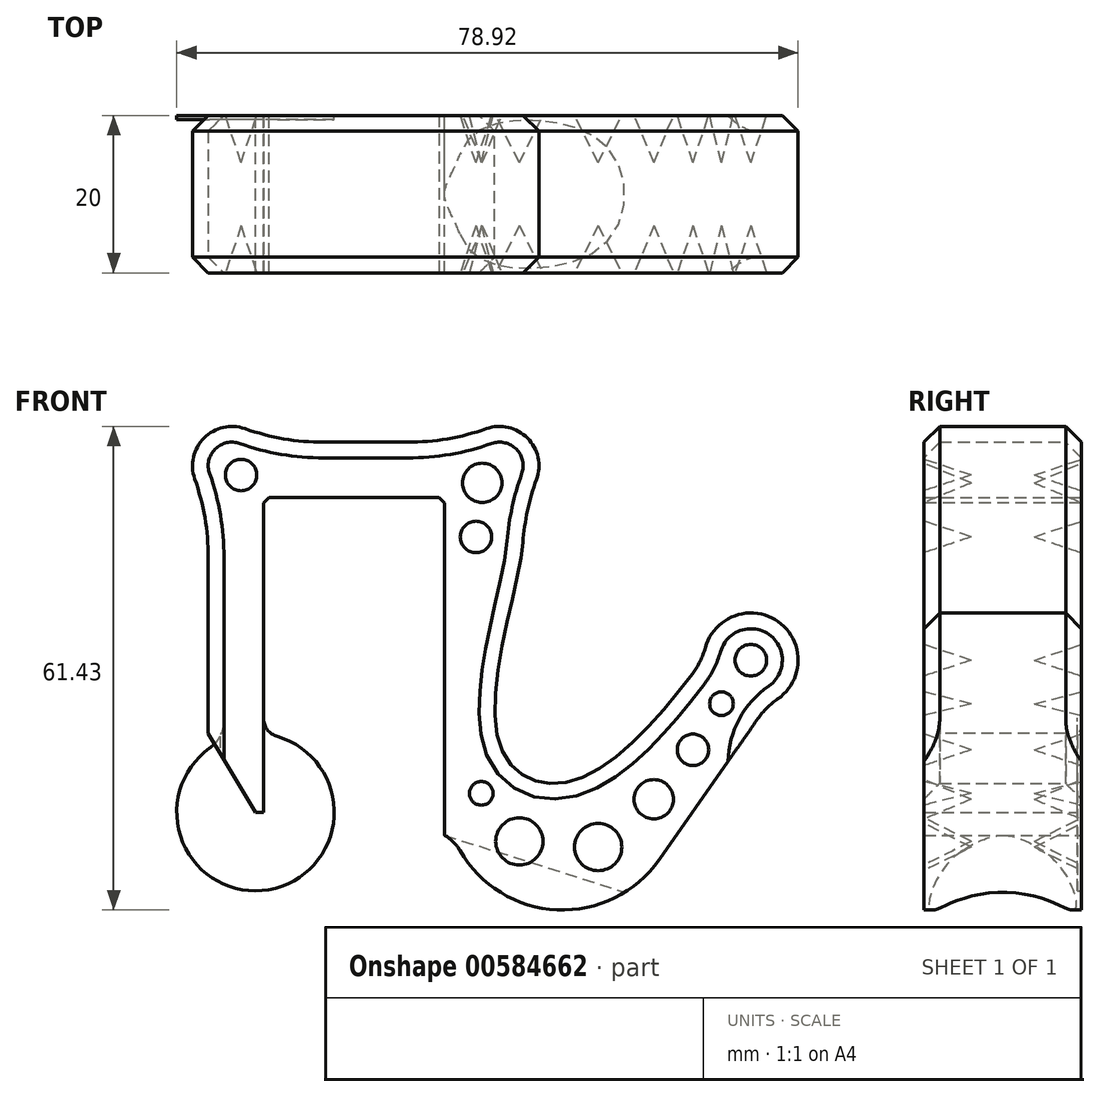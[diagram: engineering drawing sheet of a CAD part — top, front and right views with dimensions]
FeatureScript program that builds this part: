
annotation { "Feature Type Name" : "Feature", "Feature Type Description" : "" }
export const myFeature = defineFeature(function(context is Context, id is Id, definition is map)
    precondition{}
    {
        {
            var Q0;
            Q0=qCreatedBy(makeId("Front.planeOp"),FACE);
            var sketch = newSketch(context, id + "F0", { "sketchPlane" : qUnion([Q0])});
            skLineSegment(sketch, "E0", {"start": v(0, 0) * mm, "end": v(0, 40) * mm});
            skLineSegment(sketch, "E1", {"start": v(0, 40) * mm, "end": v(23, 40) * mm});
            skLineSegment(sketch, "E2", {"start": v(23, 40) * mm, "end": v(23, 2.57) * mm});
            skLineSegment(sketch, "E3", {"start": v(0, 0) * mm, "end": v(-7, 0) * mm});
            skLineSegment(sketch, "E4", {"start": v(-7, 0) * mm, "end": v(-7, 47) * mm});
            skLineSegment(sketch, "E5", {"start": v(-7, 47) * mm, "end": v(33, 47) * mm});
            skLineSegment(sketch, "E6", {"start": v(33, 47) * mm, "end": v(33, 35) * mm});
            skCircle(sketch, "E7", {"center": v(-4, 44) * mm, "radius": 5 * mm});
            skCircle(sketch, "E8", {"center": v(30, 44) * mm, "radius": 5 * mm});
            skLineSegment(sketch, "E9", {"start": v(66.02, 16.44) * mm, "end": v(50.29, -6.03) * mm});
            skCircle(sketch, "E10", {"center": v(61.92, 19.3) * mm, "radius": 6 * mm});
            skPoint(sketch, "E10.second.point", {"position": v(57, 22.75) * mm});
            skPoint(sketch, "E10.third.point", {"position": v(65.36, 24.22) * mm});
            skLineSegment(sketch, "E11", {"start": v(61.92, 19.3) * mm, "end": v(66.02, 16.44) * mm, "construction": true});
            skLineSegment(sketch, "E12", {"start": v(57, 22.75) * mm, "end": v(61.92, 19.3) * mm, "construction": true});
            skLineSegment(sketch, "E13", {"start": v(65.36, 24.22) * mm, "end": v(61.92, 19.3) * mm, "construction": true});
            skFitSpline(sketch, "E14", {"points": [v(33, 35) * mm, v(29.83, 9.17) * mm, v(39.83, 4.17) * mm, v(57.83, 22.17) * mm], "startDerivative": vector(0, -39.67) * mm, "endDerivative": vector(32.2, 46) * mm});
            skPoint(sketch, "E15.visualSharp", {"position": v(23, -45) * mm});
            skArc(sketch, "E15.filletArc", {"start": v(23, 2.57) * mm, "mid": v(33.49, -11.73) * mm, "end": v(50.29, -6.03) * mm});
            skPoint(sketch, "E16", {"position": v(0, 47) * mm});
            skLineSegment(sketch, "E17", {"start": v(53.81, 16.44) * mm, "end": v(57.83, 22.17) * mm, "construction": true});
            skLineSegment(sketch, "E18", {"start": v(33, 30) * mm, "end": v(33, 35) * mm, "construction": true});
            skLineSegment(sketch, "E19", {"start": v(12, -11) * mm, "end": v(50.15, -23.03) * mm});
            skLineSegment(sketch, "E20", {"start": v(50.15, -23.03) * mm, "end": v(53.46, -12.54) * mm});
            skLineSegment(sketch, "E21", {"start": v(53.46, -12.54) * mm, "end": v(15.3, -0.5) * mm});
            skLineSegment(sketch, "E22", {"start": v(15.3, -0.5) * mm, "end": v(12, -11) * mm});
            skLineSegment(sketch, "E23", {"start": v(12, -11) * mm, "end": v(12, 0) * mm, "construction": true});
            skLineSegment(sketch, "E24", {"start": v(23, 2.57) * mm, "end": v(23, -12.43) * mm});
            skLineSegment(sketch, "E25", {"start": v(23, -12.43) * mm, "end": v(25, -12.43) * mm});
            skArc(sketch, "E26", {"start": v(30.06, -10.15) * mm, "mid": v(27.19, -10.52) * mm, "end": v(25, -12.43) * mm});
            skSolve(sketch);
        }
        {
            var Q0;
            {var subQ0=sQuery(id+"F0.wireOp",EDGE,"E5");var subQ1=sQuery(id+"F0.wireOp",EDGE,"E4");var subQ2=makeQuery(id+"F0.imprint","INTERSECT",VERTEX,{"derivedFrom":[subQ1,subQ0]});Q0=makeQuery(id+"F0.imprint","IMPRINT",FACE,{"disambiguationData":[TD([[makeQuery(id+"F0.imprint","IMPRINT",EDGE,{"disambiguationData":[TD([[subQ2,1.0]])],"derivedFrom":subQ1}),1.0]])]});}
            var Q1;
            {var subQ0=sQuery(id+"F0.wireOp",EDGE,"E6");var subQ1=sQuery(id+"F0.wireOp",EDGE,"E5");var subQ2=makeQuery(id+"F0.imprint","INTERSECT",VERTEX,{"derivedFrom":[subQ1,subQ0]});Q1=makeQuery(id+"F0.imprint","IMPRINT",FACE,{"disambiguationData":[TD([[makeQuery(id+"F0.imprint","IMPRINT",EDGE,{"disambiguationData":[TD([[subQ2,1.0]])],"derivedFrom":subQ1}),1.0]])]});}
            var Q2;
            {var subQ0=sQuery(id+"F0.wireOp",EDGE,"E10");var subQ1=makeQuery(id+"F0.imprint","INTERSECT",VERTEX,{"derivedFrom":[sQuery(id+"F0.wireOp",EDGE,"E9"),subQ0]});Q2=makeQuery(id+"F0.imprint","IMPRINT",FACE,{"disambiguationData":[TD([[makeQuery(id+"F0.imprint","IMPRINT",EDGE,{"disambiguationData":[TD([[subQ1,1.0]])],"derivedFrom":subQ0}),1.0]])]});}
            var Q3;
            {var subQ0=sQuery(id+"F0.wireOp",EDGE,"E15.filletArc");Q3=makeQuery(id+"F0.imprint","IMPRINT",FACE,{"disambiguationData":[TD([[makeQuery(id+"F0.imprint","IMPRINT",EDGE,{"derivedFrom":subQ0}),1.0]])]});}
            var Q4;
            {var subQ0=sQuery(id+"F0.wireOp",EDGE,"E5");var subQ1=sQuery(id+"F0.wireOp",EDGE,"E4");var subQ2=makeQuery(id+"F0.imprint","INTERSECT",VERTEX,{"derivedFrom":[subQ1,subQ0]});Q4=makeQuery(id+"F0.imprint","IMPRINT",FACE,{"disambiguationData":[TD([[makeQuery(id+"F0.imprint","IMPRINT",EDGE,{"disambiguationData":[TD([[subQ2,1.0]])],"derivedFrom":subQ1}),-1.0]])]});}
            var Q5;
            {var subQ0=sQuery(id+"F0.wireOp",EDGE,"E6");var subQ1=sQuery(id+"F0.wireOp",EDGE,"E5");var subQ2=makeQuery(id+"F0.imprint","INTERSECT",VERTEX,{"derivedFrom":[subQ1,subQ0]});Q5=makeQuery(id+"F0.imprint","IMPRINT",FACE,{"disambiguationData":[TD([[makeQuery(id+"F0.imprint","IMPRINT",EDGE,{"disambiguationData":[TD([[subQ2,1.0]])],"derivedFrom":subQ1}),-1.0]])]});}
            var Q6;
            Q6=makeQuery(id+"F0.imprint","IMPRINT",FACE,{"disambiguationData":[TD([[makeQuery(id+"F0.imprint","IMPRINT",EDGE,{"derivedFrom":sQuery(id+"F0.wireOp",EDGE,"E0")}),1.0]])]});
            var Q7;
            {var subQ0=sQuery(id+"F0.wireOp",EDGE,"E24");var subQ3=sQuery(id+"F0.wireOp",EDGE,"E21");var subQ5=makeQuery(id+"F0.imprint","INTERSECT",VERTEX,{"derivedFrom":[subQ3,subQ0]});Q7=makeQuery(id+"F0.imprint","IMPRINT",FACE,{"disambiguationData":[TD([[makeQuery(id+"F0.imprint","IMPRINT",EDGE,{"disambiguationData":[TD([[subQ5,1.0]])],"derivedFrom":subQ3}),-1.0]])]});}
            extrude(context, id + "F1", {"entities" : qUnion([Q0, Q1, Q2, Q3, Q4, Q5, Q6, Q7]), "endBound" : BoundingType.SYMMETRIC, "depth" : 20 * mm, "offsetDistance" : 25 * mm});
        }
        {
            var Q0;
            Q0=makeQuery(id+"F1.opExtrude","SWEPT_EDGE",EDGE,{"disambiguationData":[OSD([sQuery(id+"F0.wireOp",EDGE,"E4"),sQuery(id+"F0.wireOp",EDGE,"E7")])]});
            var Q1;
            Q1=makeQuery(id+"F1.opExtrude","SWEPT_EDGE",EDGE,{"disambiguationData":[OSD([sQuery(id+"F0.wireOp",EDGE,"E5"),sQuery(id+"F0.wireOp",EDGE,"E7")])]});
            var Q2;
            Q2=makeQuery(id+"F1.opExtrude","SWEPT_EDGE",EDGE,{"disambiguationData":[OSD([sQuery(id+"F0.wireOp",EDGE,"E5"),sQuery(id+"F0.wireOp",EDGE,"E8")])]});
            var Q3;
            Q3=makeQuery(id+"F1.opExtrude","SWEPT_EDGE",EDGE,{"disambiguationData":[OSD([sQuery(id+"F0.wireOp",EDGE,"E6"),sQuery(id+"F0.wireOp",EDGE,"E8")])]});
            fillet(context, id + "F2", {"entities" : qUnion([Q0, Q1, Q2, Q3]), "radius" : 30 * mm, "tangentPropagation" : true, "allowEdgeOverflow" : false});
        }
        {
            var Q0;
            Q0=makeQuery(id+"F1.opExtrude","SWEPT_EDGE",EDGE,{"disambiguationData":[OSD([sQuery(id+"F0.wireOp",EDGE,"E10"),sQuery(id+"F0.wireOp",EDGE,"E14")])]});
            var Q1;
            Q1=makeQuery(id+"F1.opExtrude","SWEPT_EDGE",EDGE,{"disambiguationData":[OSD([sQuery(id+"F0.wireOp",EDGE,"E9"),sQuery(id+"F0.wireOp",EDGE,"E10")])]});
            fillet(context, id + "F3", {"entities" : qUnion([Q0, Q1]), "radius" : 10 * mm, "tangentPropagation" : true, "allowEdgeOverflow" : false});
        }
        {
            var Q0;
            {var subQ0=sQuery(id+"F0.wireOp",EDGE,"E7");var subQ1=sQuery(id+"F0.wireOp",EDGE,"E4");Q0=makeQuery(id+"F2.opFillet","BLEND_EDGE",EDGE,{"blendedFrom":[makeQuery(id+"F1.opExtrude","SWEPT_EDGE",EDGE,{"disambiguationData":[OSD([subQ1,subQ0])]}),makeQuery(id+"F1.opExtrude","CAP_FACE",FACE,{"disambiguationData":[OSD([sQuery(id+"F0.wireOp",EDGE,"E0"),sQuery(id+"F0.wireOp",EDGE,"E1"),sQuery(id+"F0.wireOp",EDGE,"E2"),sQuery(id+"F0.wireOp",EDGE,"E3"),subQ1,sQuery(id+"F0.wireOp",EDGE,"E5"),sQuery(id+"F0.wireOp",EDGE,"E6"),subQ0,sQuery(id+"F0.wireOp",EDGE,"E8"),sQuery(id+"F0.wireOp",EDGE,"E9"),sQuery(id+"F0.wireOp",EDGE,"E10"),sQuery(id+"F0.wireOp",EDGE,"E14"),sQuery(id+"F0.wireOp",EDGE,"E15.filletArc")])],"isStart":false})],"blendedInto":[makeQuery(id+"F1.opExtrude","CAP_FACE",FACE,{"disambiguationData":[OSD([sQuery(id+"F0.wireOp",EDGE,"E0"),sQuery(id+"F0.wireOp",EDGE,"E1"),sQuery(id+"F0.wireOp",EDGE,"E2"),sQuery(id+"F0.wireOp",EDGE,"E3"),subQ1,sQuery(id+"F0.wireOp",EDGE,"E5"),sQuery(id+"F0.wireOp",EDGE,"E6"),subQ0,sQuery(id+"F0.wireOp",EDGE,"E8"),sQuery(id+"F0.wireOp",EDGE,"E9"),sQuery(id+"F0.wireOp",EDGE,"E10"),sQuery(id+"F0.wireOp",EDGE,"E14"),sQuery(id+"F0.wireOp",EDGE,"E15.filletArc")])],"isStart":false})]});}
            var Q1;
            {var subQ0=sQuery(id+"F0.wireOp",EDGE,"E7");var subQ1=sQuery(id+"F0.wireOp",EDGE,"E4");Q1=makeQuery(id+"F2.opFillet","BLEND_EDGE",EDGE,{"blendedFrom":[makeQuery(id+"F1.opExtrude","SWEPT_EDGE",EDGE,{"disambiguationData":[OSD([subQ1,subQ0])]}),makeQuery(id+"F1.opExtrude","CAP_FACE",FACE,{"disambiguationData":[OSD([sQuery(id+"F0.wireOp",EDGE,"E0"),sQuery(id+"F0.wireOp",EDGE,"E1"),sQuery(id+"F0.wireOp",EDGE,"E2"),sQuery(id+"F0.wireOp",EDGE,"E3"),subQ1,sQuery(id+"F0.wireOp",EDGE,"E5"),sQuery(id+"F0.wireOp",EDGE,"E6"),subQ0,sQuery(id+"F0.wireOp",EDGE,"E8"),sQuery(id+"F0.wireOp",EDGE,"E9"),sQuery(id+"F0.wireOp",EDGE,"E10"),sQuery(id+"F0.wireOp",EDGE,"E14"),sQuery(id+"F0.wireOp",EDGE,"E15.filletArc")])],"isStart":true})],"blendedInto":[makeQuery(id+"F1.opExtrude","CAP_FACE",FACE,{"disambiguationData":[OSD([sQuery(id+"F0.wireOp",EDGE,"E0"),sQuery(id+"F0.wireOp",EDGE,"E1"),sQuery(id+"F0.wireOp",EDGE,"E2"),sQuery(id+"F0.wireOp",EDGE,"E3"),subQ1,sQuery(id+"F0.wireOp",EDGE,"E5"),sQuery(id+"F0.wireOp",EDGE,"E6"),subQ0,sQuery(id+"F0.wireOp",EDGE,"E8"),sQuery(id+"F0.wireOp",EDGE,"E9"),sQuery(id+"F0.wireOp",EDGE,"E10"),sQuery(id+"F0.wireOp",EDGE,"E14"),sQuery(id+"F0.wireOp",EDGE,"E15.filletArc")])],"isStart":true})]});}
            var Q2;
            Q2=makeQuery(id+"F1.opExtrude","CAP_EDGE",EDGE,{"disambiguationData":[OSD([sQuery(id+"F0.wireOp",EDGE,"E7")])],"isStart":false});
            var Q3;
            {var subQ0=sQuery(id+"F0.wireOp",EDGE,"E7");var subQ1=sQuery(id+"F0.wireOp",EDGE,"E5");Q3=makeQuery(id+"F2.opFillet","BLEND_EDGE",EDGE,{"blendedFrom":[makeQuery(id+"F1.opExtrude","SWEPT_EDGE",EDGE,{"disambiguationData":[OSD([subQ1,subQ0])]}),makeQuery(id+"F1.opExtrude","CAP_FACE",FACE,{"disambiguationData":[OSD([sQuery(id+"F0.wireOp",EDGE,"E0"),sQuery(id+"F0.wireOp",EDGE,"E1"),sQuery(id+"F0.wireOp",EDGE,"E2"),sQuery(id+"F0.wireOp",EDGE,"E3"),sQuery(id+"F0.wireOp",EDGE,"E4"),subQ1,sQuery(id+"F0.wireOp",EDGE,"E6"),subQ0,sQuery(id+"F0.wireOp",EDGE,"E8"),sQuery(id+"F0.wireOp",EDGE,"E9"),sQuery(id+"F0.wireOp",EDGE,"E10"),sQuery(id+"F0.wireOp",EDGE,"E14"),sQuery(id+"F0.wireOp",EDGE,"E15.filletArc")])],"isStart":false})],"blendedInto":[makeQuery(id+"F1.opExtrude","CAP_FACE",FACE,{"disambiguationData":[OSD([sQuery(id+"F0.wireOp",EDGE,"E0"),sQuery(id+"F0.wireOp",EDGE,"E1"),sQuery(id+"F0.wireOp",EDGE,"E2"),sQuery(id+"F0.wireOp",EDGE,"E3"),sQuery(id+"F0.wireOp",EDGE,"E4"),subQ1,sQuery(id+"F0.wireOp",EDGE,"E6"),subQ0,sQuery(id+"F0.wireOp",EDGE,"E8"),sQuery(id+"F0.wireOp",EDGE,"E9"),sQuery(id+"F0.wireOp",EDGE,"E10"),sQuery(id+"F0.wireOp",EDGE,"E14"),sQuery(id+"F0.wireOp",EDGE,"E15.filletArc")])],"isStart":false})]});}
            var Q4;
            Q4=makeQuery(id+"F1.opExtrude","CAP_EDGE",EDGE,{"disambiguationData":[OSD([sQuery(id+"F0.wireOp",EDGE,"E8")])],"isStart":false});
            var Q5;
            {var subQ0=sQuery(id+"F0.wireOp",EDGE,"E8");var subQ1=sQuery(id+"F0.wireOp",EDGE,"E6");Q5=makeQuery(id+"F2.opFillet","BLEND_EDGE",EDGE,{"blendedFrom":[makeQuery(id+"F1.opExtrude","SWEPT_EDGE",EDGE,{"disambiguationData":[OSD([subQ1,subQ0])]}),makeQuery(id+"F1.opExtrude","CAP_FACE",FACE,{"disambiguationData":[OSD([sQuery(id+"F0.wireOp",EDGE,"E0"),sQuery(id+"F0.wireOp",EDGE,"E1"),sQuery(id+"F0.wireOp",EDGE,"E2"),sQuery(id+"F0.wireOp",EDGE,"E3"),sQuery(id+"F0.wireOp",EDGE,"E4"),sQuery(id+"F0.wireOp",EDGE,"E5"),subQ1,sQuery(id+"F0.wireOp",EDGE,"E7"),subQ0,sQuery(id+"F0.wireOp",EDGE,"E9"),sQuery(id+"F0.wireOp",EDGE,"E10"),sQuery(id+"F0.wireOp",EDGE,"E14"),sQuery(id+"F0.wireOp",EDGE,"E15.filletArc")])],"isStart":false})],"blendedInto":[makeQuery(id+"F1.opExtrude","CAP_FACE",FACE,{"disambiguationData":[OSD([sQuery(id+"F0.wireOp",EDGE,"E0"),sQuery(id+"F0.wireOp",EDGE,"E1"),sQuery(id+"F0.wireOp",EDGE,"E2"),sQuery(id+"F0.wireOp",EDGE,"E3"),sQuery(id+"F0.wireOp",EDGE,"E4"),sQuery(id+"F0.wireOp",EDGE,"E5"),subQ1,sQuery(id+"F0.wireOp",EDGE,"E7"),subQ0,sQuery(id+"F0.wireOp",EDGE,"E9"),sQuery(id+"F0.wireOp",EDGE,"E10"),sQuery(id+"F0.wireOp",EDGE,"E14"),sQuery(id+"F0.wireOp",EDGE,"E15.filletArc")])],"isStart":false})]});}
            var Q6;
            Q6=makeQuery(id+"F1.opExtrude","CAP_EDGE",EDGE,{"disambiguationData":[OSD([sQuery(id+"F0.wireOp",EDGE,"E14")])],"isStart":false});
            var Q7;
            {var subQ0=sQuery(id+"F0.wireOp",EDGE,"E8");var subQ1=sQuery(id+"F0.wireOp",EDGE,"E5");Q7=makeQuery(id+"F2.opFillet","BLEND_EDGE",EDGE,{"blendedFrom":[makeQuery(id+"F1.opExtrude","SWEPT_EDGE",EDGE,{"disambiguationData":[OSD([subQ1,subQ0])]}),makeQuery(id+"F1.opExtrude","CAP_FACE",FACE,{"disambiguationData":[OSD([sQuery(id+"F0.wireOp",EDGE,"E0"),sQuery(id+"F0.wireOp",EDGE,"E1"),sQuery(id+"F0.wireOp",EDGE,"E2"),sQuery(id+"F0.wireOp",EDGE,"E3"),sQuery(id+"F0.wireOp",EDGE,"E4"),subQ1,sQuery(id+"F0.wireOp",EDGE,"E6"),sQuery(id+"F0.wireOp",EDGE,"E7"),subQ0,sQuery(id+"F0.wireOp",EDGE,"E9"),sQuery(id+"F0.wireOp",EDGE,"E10"),sQuery(id+"F0.wireOp",EDGE,"E14"),sQuery(id+"F0.wireOp",EDGE,"E15.filletArc")])],"isStart":false})],"blendedInto":[makeQuery(id+"F1.opExtrude","CAP_FACE",FACE,{"disambiguationData":[OSD([sQuery(id+"F0.wireOp",EDGE,"E0"),sQuery(id+"F0.wireOp",EDGE,"E1"),sQuery(id+"F0.wireOp",EDGE,"E2"),sQuery(id+"F0.wireOp",EDGE,"E3"),sQuery(id+"F0.wireOp",EDGE,"E4"),subQ1,sQuery(id+"F0.wireOp",EDGE,"E6"),sQuery(id+"F0.wireOp",EDGE,"E7"),subQ0,sQuery(id+"F0.wireOp",EDGE,"E9"),sQuery(id+"F0.wireOp",EDGE,"E10"),sQuery(id+"F0.wireOp",EDGE,"E14"),sQuery(id+"F0.wireOp",EDGE,"E15.filletArc")])],"isStart":false})]});}
            var Q8;
            Q8=makeQuery(id+"F1.opExtrude","CAP_EDGE",EDGE,{"disambiguationData":[OSD([sQuery(id+"F0.wireOp",EDGE,"E10")])],"isStart":false});
            var Q9;
            {var subQ0=sQuery(id+"F0.wireOp",EDGE,"E14");var subQ1=sQuery(id+"F0.wireOp",EDGE,"E10");Q9=makeQuery(id+"F3.opFillet","BLEND_EDGE",EDGE,{"blendedFrom":[makeQuery(id+"F1.opExtrude","SWEPT_EDGE",EDGE,{"disambiguationData":[OSD([subQ1,subQ0])]}),makeQuery(id+"F1.opExtrude","CAP_FACE",FACE,{"disambiguationData":[OSD([sQuery(id+"F0.wireOp",EDGE,"E0"),sQuery(id+"F0.wireOp",EDGE,"E1"),sQuery(id+"F0.wireOp",EDGE,"E2"),sQuery(id+"F0.wireOp",EDGE,"E3"),sQuery(id+"F0.wireOp",EDGE,"E4"),sQuery(id+"F0.wireOp",EDGE,"E5"),sQuery(id+"F0.wireOp",EDGE,"E6"),sQuery(id+"F0.wireOp",EDGE,"E7"),sQuery(id+"F0.wireOp",EDGE,"E8"),sQuery(id+"F0.wireOp",EDGE,"E9"),subQ1,subQ0,sQuery(id+"F0.wireOp",EDGE,"E15.filletArc")])],"isStart":false})],"blendedInto":[makeQuery(id+"F1.opExtrude","CAP_FACE",FACE,{"disambiguationData":[OSD([sQuery(id+"F0.wireOp",EDGE,"E0"),sQuery(id+"F0.wireOp",EDGE,"E1"),sQuery(id+"F0.wireOp",EDGE,"E2"),sQuery(id+"F0.wireOp",EDGE,"E3"),sQuery(id+"F0.wireOp",EDGE,"E4"),sQuery(id+"F0.wireOp",EDGE,"E5"),sQuery(id+"F0.wireOp",EDGE,"E6"),sQuery(id+"F0.wireOp",EDGE,"E7"),sQuery(id+"F0.wireOp",EDGE,"E8"),sQuery(id+"F0.wireOp",EDGE,"E9"),subQ1,subQ0,sQuery(id+"F0.wireOp",EDGE,"E15.filletArc")])],"isStart":false})]});}
            var Q10;
            {var subQ0=sQuery(id+"F0.wireOp",EDGE,"E10");var subQ1=sQuery(id+"F0.wireOp",EDGE,"E9");Q10=makeQuery(id+"F3.opFillet","BLEND_EDGE",EDGE,{"blendedFrom":[makeQuery(id+"F1.opExtrude","SWEPT_EDGE",EDGE,{"disambiguationData":[OSD([subQ1,subQ0])]}),makeQuery(id+"F1.opExtrude","CAP_FACE",FACE,{"disambiguationData":[OSD([sQuery(id+"F0.wireOp",EDGE,"E0"),sQuery(id+"F0.wireOp",EDGE,"E1"),sQuery(id+"F0.wireOp",EDGE,"E2"),sQuery(id+"F0.wireOp",EDGE,"E3"),sQuery(id+"F0.wireOp",EDGE,"E4"),sQuery(id+"F0.wireOp",EDGE,"E5"),sQuery(id+"F0.wireOp",EDGE,"E6"),sQuery(id+"F0.wireOp",EDGE,"E7"),sQuery(id+"F0.wireOp",EDGE,"E8"),subQ1,subQ0,sQuery(id+"F0.wireOp",EDGE,"E14"),sQuery(id+"F0.wireOp",EDGE,"E15.filletArc")])],"isStart":false})],"blendedInto":[makeQuery(id+"F1.opExtrude","CAP_FACE",FACE,{"disambiguationData":[OSD([sQuery(id+"F0.wireOp",EDGE,"E0"),sQuery(id+"F0.wireOp",EDGE,"E1"),sQuery(id+"F0.wireOp",EDGE,"E2"),sQuery(id+"F0.wireOp",EDGE,"E3"),sQuery(id+"F0.wireOp",EDGE,"E4"),sQuery(id+"F0.wireOp",EDGE,"E5"),sQuery(id+"F0.wireOp",EDGE,"E6"),sQuery(id+"F0.wireOp",EDGE,"E7"),sQuery(id+"F0.wireOp",EDGE,"E8"),subQ1,subQ0,sQuery(id+"F0.wireOp",EDGE,"E14"),sQuery(id+"F0.wireOp",EDGE,"E15.filletArc")])],"isStart":false})]});}
            var Q11;
            {var subQ0=sQuery(id+"F0.wireOp",EDGE,"E10");var subQ1=sQuery(id+"F0.wireOp",EDGE,"E9");Q11=makeQuery(id+"F3.opFillet","BLEND_EDGE",EDGE,{"blendedFrom":[makeQuery(id+"F1.opExtrude","SWEPT_EDGE",EDGE,{"disambiguationData":[OSD([subQ1,subQ0])]}),makeQuery(id+"F1.opExtrude","CAP_FACE",FACE,{"disambiguationData":[OSD([sQuery(id+"F0.wireOp",EDGE,"E0"),sQuery(id+"F0.wireOp",EDGE,"E1"),sQuery(id+"F0.wireOp",EDGE,"E2"),sQuery(id+"F0.wireOp",EDGE,"E3"),sQuery(id+"F0.wireOp",EDGE,"E4"),sQuery(id+"F0.wireOp",EDGE,"E5"),sQuery(id+"F0.wireOp",EDGE,"E6"),sQuery(id+"F0.wireOp",EDGE,"E7"),sQuery(id+"F0.wireOp",EDGE,"E8"),subQ1,subQ0,sQuery(id+"F0.wireOp",EDGE,"E14"),sQuery(id+"F0.wireOp",EDGE,"E15.filletArc")])],"isStart":true})],"blendedInto":[makeQuery(id+"F1.opExtrude","CAP_FACE",FACE,{"disambiguationData":[OSD([sQuery(id+"F0.wireOp",EDGE,"E0"),sQuery(id+"F0.wireOp",EDGE,"E1"),sQuery(id+"F0.wireOp",EDGE,"E2"),sQuery(id+"F0.wireOp",EDGE,"E3"),sQuery(id+"F0.wireOp",EDGE,"E4"),sQuery(id+"F0.wireOp",EDGE,"E5"),sQuery(id+"F0.wireOp",EDGE,"E6"),sQuery(id+"F0.wireOp",EDGE,"E7"),sQuery(id+"F0.wireOp",EDGE,"E8"),subQ1,subQ0,sQuery(id+"F0.wireOp",EDGE,"E14"),sQuery(id+"F0.wireOp",EDGE,"E15.filletArc")])],"isStart":true})]});}
            var Q12;
            Q12=makeQuery(id+"F1.opExtrude","CAP_EDGE",EDGE,{"disambiguationData":[OSD([sQuery(id+"F0.wireOp",EDGE,"E10")])],"isStart":true});
            var Q13;
            Q13=makeQuery(id+"F1.opExtrude","CAP_EDGE",EDGE,{"disambiguationData":[OSD([sQuery(id+"F0.wireOp",EDGE,"E14")])],"isStart":true});
            var Q14;
            {var subQ0=sQuery(id+"F0.wireOp",EDGE,"E14");var subQ1=sQuery(id+"F0.wireOp",EDGE,"E10");Q14=makeQuery(id+"F3.opFillet","BLEND_EDGE",EDGE,{"blendedFrom":[makeQuery(id+"F1.opExtrude","SWEPT_EDGE",EDGE,{"disambiguationData":[OSD([subQ1,subQ0])]}),makeQuery(id+"F1.opExtrude","CAP_FACE",FACE,{"disambiguationData":[OSD([sQuery(id+"F0.wireOp",EDGE,"E0"),sQuery(id+"F0.wireOp",EDGE,"E1"),sQuery(id+"F0.wireOp",EDGE,"E2"),sQuery(id+"F0.wireOp",EDGE,"E3"),sQuery(id+"F0.wireOp",EDGE,"E4"),sQuery(id+"F0.wireOp",EDGE,"E5"),sQuery(id+"F0.wireOp",EDGE,"E6"),sQuery(id+"F0.wireOp",EDGE,"E7"),sQuery(id+"F0.wireOp",EDGE,"E8"),sQuery(id+"F0.wireOp",EDGE,"E9"),subQ1,subQ0,sQuery(id+"F0.wireOp",EDGE,"E15.filletArc")])],"isStart":true})],"blendedInto":[makeQuery(id+"F1.opExtrude","CAP_FACE",FACE,{"disambiguationData":[OSD([sQuery(id+"F0.wireOp",EDGE,"E0"),sQuery(id+"F0.wireOp",EDGE,"E1"),sQuery(id+"F0.wireOp",EDGE,"E2"),sQuery(id+"F0.wireOp",EDGE,"E3"),sQuery(id+"F0.wireOp",EDGE,"E4"),sQuery(id+"F0.wireOp",EDGE,"E5"),sQuery(id+"F0.wireOp",EDGE,"E6"),sQuery(id+"F0.wireOp",EDGE,"E7"),sQuery(id+"F0.wireOp",EDGE,"E8"),sQuery(id+"F0.wireOp",EDGE,"E9"),subQ1,subQ0,sQuery(id+"F0.wireOp",EDGE,"E15.filletArc")])],"isStart":true})]});}
            var Q15;
            {var subQ0=sQuery(id+"F0.wireOp",EDGE,"E8");var subQ1=sQuery(id+"F0.wireOp",EDGE,"E6");Q15=makeQuery(id+"F2.opFillet","BLEND_EDGE",EDGE,{"blendedFrom":[makeQuery(id+"F1.opExtrude","SWEPT_EDGE",EDGE,{"disambiguationData":[OSD([subQ1,subQ0])]}),makeQuery(id+"F1.opExtrude","CAP_FACE",FACE,{"disambiguationData":[OSD([sQuery(id+"F0.wireOp",EDGE,"E0"),sQuery(id+"F0.wireOp",EDGE,"E1"),sQuery(id+"F0.wireOp",EDGE,"E2"),sQuery(id+"F0.wireOp",EDGE,"E3"),sQuery(id+"F0.wireOp",EDGE,"E4"),sQuery(id+"F0.wireOp",EDGE,"E5"),subQ1,sQuery(id+"F0.wireOp",EDGE,"E7"),subQ0,sQuery(id+"F0.wireOp",EDGE,"E9"),sQuery(id+"F0.wireOp",EDGE,"E10"),sQuery(id+"F0.wireOp",EDGE,"E14"),sQuery(id+"F0.wireOp",EDGE,"E15.filletArc")])],"isStart":true})],"blendedInto":[makeQuery(id+"F1.opExtrude","CAP_FACE",FACE,{"disambiguationData":[OSD([sQuery(id+"F0.wireOp",EDGE,"E0"),sQuery(id+"F0.wireOp",EDGE,"E1"),sQuery(id+"F0.wireOp",EDGE,"E2"),sQuery(id+"F0.wireOp",EDGE,"E3"),sQuery(id+"F0.wireOp",EDGE,"E4"),sQuery(id+"F0.wireOp",EDGE,"E5"),subQ1,sQuery(id+"F0.wireOp",EDGE,"E7"),subQ0,sQuery(id+"F0.wireOp",EDGE,"E9"),sQuery(id+"F0.wireOp",EDGE,"E10"),sQuery(id+"F0.wireOp",EDGE,"E14"),sQuery(id+"F0.wireOp",EDGE,"E15.filletArc")])],"isStart":true})]});}
            var Q16;
            Q16=makeQuery(id+"F1.opExtrude","CAP_EDGE",EDGE,{"disambiguationData":[OSD([sQuery(id+"F0.wireOp",EDGE,"E8")])],"isStart":true});
            var Q17;
            {var subQ0=sQuery(id+"F0.wireOp",EDGE,"E8");var subQ1=sQuery(id+"F0.wireOp",EDGE,"E5");Q17=makeQuery(id+"F2.opFillet","BLEND_EDGE",EDGE,{"blendedFrom":[makeQuery(id+"F1.opExtrude","SWEPT_EDGE",EDGE,{"disambiguationData":[OSD([subQ1,subQ0])]}),makeQuery(id+"F1.opExtrude","CAP_FACE",FACE,{"disambiguationData":[OSD([sQuery(id+"F0.wireOp",EDGE,"E0"),sQuery(id+"F0.wireOp",EDGE,"E1"),sQuery(id+"F0.wireOp",EDGE,"E2"),sQuery(id+"F0.wireOp",EDGE,"E3"),sQuery(id+"F0.wireOp",EDGE,"E4"),subQ1,sQuery(id+"F0.wireOp",EDGE,"E6"),sQuery(id+"F0.wireOp",EDGE,"E7"),subQ0,sQuery(id+"F0.wireOp",EDGE,"E9"),sQuery(id+"F0.wireOp",EDGE,"E10"),sQuery(id+"F0.wireOp",EDGE,"E14"),sQuery(id+"F0.wireOp",EDGE,"E15.filletArc")])],"isStart":true})],"blendedInto":[makeQuery(id+"F1.opExtrude","CAP_FACE",FACE,{"disambiguationData":[OSD([sQuery(id+"F0.wireOp",EDGE,"E0"),sQuery(id+"F0.wireOp",EDGE,"E1"),sQuery(id+"F0.wireOp",EDGE,"E2"),sQuery(id+"F0.wireOp",EDGE,"E3"),sQuery(id+"F0.wireOp",EDGE,"E4"),subQ1,sQuery(id+"F0.wireOp",EDGE,"E6"),sQuery(id+"F0.wireOp",EDGE,"E7"),subQ0,sQuery(id+"F0.wireOp",EDGE,"E9"),sQuery(id+"F0.wireOp",EDGE,"E10"),sQuery(id+"F0.wireOp",EDGE,"E14"),sQuery(id+"F0.wireOp",EDGE,"E15.filletArc")])],"isStart":true})]});}
            var Q18;
            Q18=makeQuery(id+"F1.opExtrude","CAP_EDGE",EDGE,{"disambiguationData":[OSD([sQuery(id+"F0.wireOp",EDGE,"E4")])],"isStart":false});
            var Q19;
            Q19=makeQuery(id+"F1.opExtrude","CAP_EDGE",EDGE,{"disambiguationData":[OSD([sQuery(id+"F0.wireOp",EDGE,"E4")])],"isStart":true});
            var Q20;
            Q20=makeQuery(id+"F1.opExtrude","CAP_EDGE",EDGE,{"disambiguationData":[OSD([sQuery(id+"F0.wireOp",EDGE,"E5")])],"isStart":false});
            var Q21;
            Q21=makeQuery(id+"F1.opExtrude","CAP_EDGE",EDGE,{"disambiguationData":[OSD([sQuery(id+"F0.wireOp",EDGE,"E5")])],"isStart":true});
            var Q22;
            {var subQ0=sQuery(id+"F0.wireOp",EDGE,"E7");var subQ1=sQuery(id+"F0.wireOp",EDGE,"E5");Q22=makeQuery(id+"F2.opFillet","BLEND_EDGE",EDGE,{"blendedFrom":[makeQuery(id+"F1.opExtrude","SWEPT_EDGE",EDGE,{"disambiguationData":[OSD([subQ1,subQ0])]}),makeQuery(id+"F1.opExtrude","CAP_FACE",FACE,{"disambiguationData":[OSD([sQuery(id+"F0.wireOp",EDGE,"E0"),sQuery(id+"F0.wireOp",EDGE,"E1"),sQuery(id+"F0.wireOp",EDGE,"E2"),sQuery(id+"F0.wireOp",EDGE,"E3"),sQuery(id+"F0.wireOp",EDGE,"E4"),subQ1,sQuery(id+"F0.wireOp",EDGE,"E6"),subQ0,sQuery(id+"F0.wireOp",EDGE,"E8"),sQuery(id+"F0.wireOp",EDGE,"E9"),sQuery(id+"F0.wireOp",EDGE,"E10"),sQuery(id+"F0.wireOp",EDGE,"E14"),sQuery(id+"F0.wireOp",EDGE,"E15.filletArc"),sQuery(id+"F0.wireOp",EDGE,"E21"),sQuery(id+"F0.wireOp",EDGE,"E24")])],"isStart":true})],"blendedInto":[makeQuery(id+"F1.opExtrude","CAP_FACE",FACE,{"disambiguationData":[OSD([sQuery(id+"F0.wireOp",EDGE,"E0"),sQuery(id+"F0.wireOp",EDGE,"E1"),sQuery(id+"F0.wireOp",EDGE,"E2"),sQuery(id+"F0.wireOp",EDGE,"E3"),sQuery(id+"F0.wireOp",EDGE,"E4"),subQ1,sQuery(id+"F0.wireOp",EDGE,"E6"),subQ0,sQuery(id+"F0.wireOp",EDGE,"E8"),sQuery(id+"F0.wireOp",EDGE,"E9"),sQuery(id+"F0.wireOp",EDGE,"E10"),sQuery(id+"F0.wireOp",EDGE,"E14"),sQuery(id+"F0.wireOp",EDGE,"E15.filletArc"),sQuery(id+"F0.wireOp",EDGE,"E21"),sQuery(id+"F0.wireOp",EDGE,"E24")])],"isStart":true})]});}
            var Q23;
            Q23=makeQuery(id+"F1.opExtrude","CAP_EDGE",EDGE,{"disambiguationData":[OSD([sQuery(id+"F0.wireOp",EDGE,"E7")])],"isStart":true});
            chamfer(context, id + "F4", {"entities" : qUnion([Q0, Q1, Q2, Q3, Q4, Q5, Q6, Q7, Q8, Q9, Q10, Q11, Q12, Q13, Q14, Q15, Q16, Q17, Q18, Q19, Q20, Q21, Q22, Q23]), "width" : 2 * mm});
        }
        {
            var Q0;
            Q0=makeQuery(id+"F1.opExtrude","SWEPT_EDGE",EDGE,{"disambiguationData":[OSD([sQuery(id+"F0.wireOp",EDGE,"E3"),sQuery(id+"F0.wireOp",EDGE,"E4")])]});
            chamfer(context, id + "F5", {"entities" : qUnion([Q0]), "chamferType" : ChamferType.TWO_OFFSETS, "width1" : 6 * mm, "oppositeDirection" : false, "width2" : 10 * mm, "tangentPropagation" : true});
        }
        {
            var Q0;
            {var subQ0=sQuery(id+"F0.wireOp",EDGE,"E15.filletArc");Q0=makeQuery(id+"F0.imprint","IMPRINT",FACE,{"disambiguationData":[TD([[makeQuery(id+"F0.imprint","IMPRINT",EDGE,{"derivedFrom":subQ0}),1.0]])]});}
            var Q1;
            {var subQ0=sQuery(id+"F0.wireOp",EDGE,"E25");Q1=makeQuery(id+"F0.imprint","IMPRINT",FACE,{"disambiguationData":[TD([[makeQuery(id+"F0.imprint","IMPRINT",EDGE,{"derivedFrom":subQ0}),1.0]])]});}
            var Q2;
            Q2=makeQuery(id+"F0.imprint","IMPRINT",FACE,{"disambiguationData":[TD([[makeQuery(id+"F0.imprint","IMPRINT",EDGE,{"derivedFrom":sQuery(id+"F0.wireOp",EDGE,"E19")}),1.0]])]});
            var Q3;
            Q3=sQuery(id+"F0.wireOp",EDGE,"E19");
            revolve(context, id + "F6", {"operationType" : NewBodyOperationType.REMOVE, "entities" : qUnion([Q0, Q1, Q2]), "axis" : qUnion([Q3]), "revolveType" : RevolveType.FULL, "oppositeDirection" : true});
        }
        {
            var Q0;
            {var subQ0=sQuery(id+"F0.wireOp",EDGE,"E21");var subQ1=sQuery(id+"F0.wireOp",EDGE,"E15.filletArc");Q0=makeQuery(id+"F6.boolean.opBoolean","SPLIT",EDGE,{"disambiguationData":[TD([makeQuery(id+"F1.opExtrude","CAP_FACE",FACE,{"disambiguationData":[OSD([sQuery(id+"F0.wireOp",EDGE,"E0"),sQuery(id+"F0.wireOp",EDGE,"E1"),sQuery(id+"F0.wireOp",EDGE,"E2"),sQuery(id+"F0.wireOp",EDGE,"E3"),sQuery(id+"F0.wireOp",EDGE,"E4"),sQuery(id+"F0.wireOp",EDGE,"E5"),sQuery(id+"F0.wireOp",EDGE,"E6"),sQuery(id+"F0.wireOp",EDGE,"E7"),sQuery(id+"F0.wireOp",EDGE,"E8"),sQuery(id+"F0.wireOp",EDGE,"E9"),sQuery(id+"F0.wireOp",EDGE,"E10"),sQuery(id+"F0.wireOp",EDGE,"E14"),subQ1,subQ0,sQuery(id+"F0.wireOp",EDGE,"E24")])],"isStart":false})])],"derivedFrom":makeQuery(id+"F1.opExtrude","SWEPT_EDGE",EDGE,{"disambiguationData":[OSD([subQ1,subQ0])]})});}
            fillet(context, id + "F7", {"entities" : qUnion([Q0]), "radius" : 5 * mm, "tangentPropagation" : true, "allowEdgeOverflow" : false});
        }
        {
            var Q0;
            Q0=makeQuery(id+"F1.opExtrude","CAP_FACE",FACE,{"disambiguationData":[OSD([sQuery(id+"F0.wireOp",EDGE,"E0"),sQuery(id+"F0.wireOp",EDGE,"E1"),sQuery(id+"F0.wireOp",EDGE,"E2"),sQuery(id+"F0.wireOp",EDGE,"E3"),sQuery(id+"F0.wireOp",EDGE,"E4"),sQuery(id+"F0.wireOp",EDGE,"E5"),sQuery(id+"F0.wireOp",EDGE,"E6"),sQuery(id+"F0.wireOp",EDGE,"E7"),sQuery(id+"F0.wireOp",EDGE,"E8"),sQuery(id+"F0.wireOp",EDGE,"E9"),sQuery(id+"F0.wireOp",EDGE,"E10"),sQuery(id+"F0.wireOp",EDGE,"E14"),sQuery(id+"F0.wireOp",EDGE,"E15.filletArc"),sQuery(id+"F0.wireOp",EDGE,"E21"),sQuery(id+"F0.wireOp",EDGE,"E24")])],"isStart":false});
            var sketch = newSketch(context, id + "F8", { "sketchPlane" : qUnion([Q0])});
            skArc(sketch, "E27.0", {"start": v(64.2, 16.01) * mm, "mid": v(64.24, 22.56) * mm, "end": v(58.07, 20.37) * mm});
            skArc(sketch, "E27.1", {"start": v(58.07, 20.37) * mm, "mid": v(57.27, 18.27) * mm, "end": v(56.08, 16.35) * mm});
            skArc(sketch, "E27.2", {"start": v(59.02, 6.44) * mm, "mid": v(60.46, 11.85) * mm, "end": v(64.2, 16.01) * mm});
            skFitSpline(sketch, "E27.3", {"points": [v(56.08, 16.35) * mm, v(54.06, 13.66) * mm, v(52.13, 11.35) * mm, v(50.3, 9.42) * mm, v(47.88, 6.87) * mm, v(45.59, 4.95) * mm, v(43.42, 3.67) * mm, v(41.22, 2.36) * mm, v(39.08, 1.7) * mm, v(37, 1.65) * mm, v(35.82, 1.63) * mm, v(34.7, 1.8) * mm, v(33.65, 2.18) * mm, v(32.55, 2.56) * mm, v(31.58, 3.14) * mm, v(30.73, 3.9) * mm, v(29.62, 4.9) * mm, v(28.78, 6.14) * mm, v(28.22, 7.63) * mm, v(27.85, 8.63) * mm, v(27.6, 9.74) * mm, v(27.49, 10.95) * mm, v(27.38, 12.17) * mm, v(27.37, 13.49) * mm, v(27.46, 14.9) * mm, v(27.53, 16.05) * mm, v(27.68, 17.37) * mm, v(27.91, 18.85) * mm, v(28.2, 20.7) * mm, v(28.72, 23.3) * mm, v(29.47, 26.63) * mm, v(29.94, 28.72) * mm, v(30.22, 30) * mm, v(30.33, 30.5) * mm, v(30.68, 32.21) * mm, v(30.9, 33.52) * mm, v(30.98, 34.42) * mm]});
            skLineSegment(sketch, "E27.4", {"start": v(59.02, 6.44) * mm, "end": v(50.29, -6.03) * mm});
            skArc(sketch, "E27.5", {"start": v(30.98, 34.42) * mm, "mid": v(31.6, 38.76) * mm, "end": v(32.82, 42.97) * mm});
            skArc(sketch, "E27.6", {"start": v(32.82, 42.97) * mm, "mid": v(32.13, 46.11) * mm, "end": v(29, 46.83) * mm});
            skArc(sketch, "E27.7", {"start": v(29, 46.83) * mm, "mid": v(23.75, 45.46) * mm, "end": v(18.34, 45) * mm});
            skLineSegment(sketch, "E27.8", {"start": v(18.34, 45) * mm, "end": v(7.66, 45) * mm});
            skArc(sketch, "E27.9", {"start": v(7.66, 45) * mm, "mid": v(2.25, 45.46) * mm, "end": v(-3, 46.83) * mm});
            skArc(sketch, "E27.10", {"start": v(-3, 46.83) * mm, "mid": v(-6.12, 46.12) * mm, "end": v(-6.83, 43) * mm});
            skArc(sketch, "E27.11", {"start": v(-6.83, 43) * mm, "mid": v(-5.46, 37.75) * mm, "end": v(-5, 32.34) * mm});
            skLineSegment(sketch, "E27.12", {"start": v(-5, 32.34) * mm, "end": v(-5, 6.67) * mm});
            skLineSegment(sketch, "E27.13", {"start": v(-5, 6.67) * mm, "end": v(-1, 0) * mm});
            skLineSegment(sketch, "E27.14", {"start": v(0, 0) * mm, "end": v(-1, 0) * mm});
            skLineSegment(sketch, "E27.15", {"start": v(0, 0) * mm, "end": v(0, 40) * mm});
            skLineSegment(sketch, "E27.16", {"start": v(0, 40) * mm, "end": v(23, 40) * mm});
            skLineSegment(sketch, "E27.17", {"start": v(23, 40) * mm, "end": v(23, -2.93) * mm});
            skArc(sketch, "E27.18", {"start": v(23, -2.93) * mm, "mid": v(24.12, -3.76) * mm, "end": v(24.97, -4.86) * mm});
            skArc(sketch, "E27.19", {"start": v(24.97, -4.86) * mm, "mid": v(37.3, -12.41) * mm, "end": v(50.29, -6.03) * mm});
            skCircle(sketch, "E28", {"center": v(61.92, 19.3) * mm, "radius": 2 * mm});
            skCircle(sketch, "E29", {"center": v(27.8, 41.83) * mm, "radius": 5.14 * mm});
            skCircle(sketch, "E30", {"center": v(-2.83, 42.83) * mm, "radius": 4 * mm});
            skCircle(sketch, "E31", {"center": v(27.8, 41.83) * mm, "radius": 2.5 * mm});
            skCircle(sketch, "E32", {"center": v(-2.83, 42.83) * mm, "radius": 2 * mm});
            skCircle(sketch, "E33", {"center": v(58.2, 13.78) * mm, "radius": 1.5 * mm});
            skCircle(sketch, "E34", {"center": v(54.57, 7.92) * mm, "radius": 2 * mm});
            skCircle(sketch, "E35", {"center": v(49.6, 1.64) * mm, "radius": 2.5 * mm});
            skCircle(sketch, "E36", {"center": v(42.53, -4.44) * mm, "radius": 3 * mm});
            skCircle(sketch, "E37", {"center": v(32.52, -3.72) * mm, "radius": 3 * mm});
            skCircle(sketch, "E38", {"center": v(27.69, 2.39) * mm, "radius": 1.5 * mm});
            skCircle(sketch, "E39", {"center": v(27.01, 34.96) * mm, "radius": 2 * mm});
            skSolve(sketch);
        }
        {
            var Q0;
            Q0=makeQuery(id+"F8.imprint","IMPRINT",FACE,{"disambiguationData":[TD([[makeQuery(id+"F8.imprint","IMPRINT",EDGE,{"derivedFrom":sQuery(id+"F8.wireOp",EDGE,"E31")}),1.0]])]});
            var Q1;
            Q1=makeQuery(id+"F8.imprint","IMPRINT",FACE,{"disambiguationData":[TD([[makeQuery(id+"F8.imprint","IMPRINT",EDGE,{"derivedFrom":sQuery(id+"F8.wireOp",EDGE,"E32")}),1.0]])]});
            var Q2;
            Q2=makeQuery(id+"F8.imprint","IMPRINT",FACE,{"disambiguationData":[TD([[makeQuery(id+"F8.imprint","IMPRINT",EDGE,{"derivedFrom":sQuery(id+"F8.wireOp",EDGE,"E39")}),1.0]])]});
            var Q3;
            Q3=makeQuery(id+"F8.imprint","IMPRINT",FACE,{"disambiguationData":[TD([[makeQuery(id+"F8.imprint","IMPRINT",EDGE,{"derivedFrom":sQuery(id+"F8.wireOp",EDGE,"E28")}),1.0]])]});
            var Q4;
            Q4=makeQuery(id+"F8.imprint","IMPRINT",FACE,{"disambiguationData":[TD([[makeQuery(id+"F8.imprint","IMPRINT",EDGE,{"derivedFrom":sQuery(id+"F8.wireOp",EDGE,"E33")}),1.0]])]});
            var Q5;
            Q5=makeQuery(id+"F8.imprint","IMPRINT",FACE,{"disambiguationData":[TD([[makeQuery(id+"F8.imprint","IMPRINT",EDGE,{"derivedFrom":sQuery(id+"F8.wireOp",EDGE,"E34")}),1.0]])]});
            var Q6;
            Q6=makeQuery(id+"F8.imprint","IMPRINT",FACE,{"disambiguationData":[TD([[makeQuery(id+"F8.imprint","IMPRINT",EDGE,{"derivedFrom":sQuery(id+"F8.wireOp",EDGE,"E35")}),1.0]])]});
            var Q7;
            Q7=makeQuery(id+"F8.imprint","IMPRINT",FACE,{"disambiguationData":[TD([[makeQuery(id+"F8.imprint","IMPRINT",EDGE,{"derivedFrom":sQuery(id+"F8.wireOp",EDGE,"E36")}),1.0]])]});
            var Q8;
            Q8=makeQuery(id+"F8.imprint","IMPRINT",FACE,{"disambiguationData":[TD([[makeQuery(id+"F8.imprint","IMPRINT",EDGE,{"derivedFrom":sQuery(id+"F8.wireOp",EDGE,"E37")}),1.0]])]});
            var Q9;
            Q9=makeQuery(id+"F8.imprint","IMPRINT",FACE,{"disambiguationData":[TD([[makeQuery(id+"F8.imprint","IMPRINT",EDGE,{"derivedFrom":sQuery(id+"F8.wireOp",EDGE,"E38")}),1.0]])]});
            extrude(context, id + "F9", {"entities" : qUnion([Q0, Q1, Q2, Q3, Q4, Q5, Q6, Q7, Q8, Q9]), "oppositeDirection" : true, "depth" : 6 * mm, "offsetDistance" : 25 * mm});
        }
        {
            var Q0;
            Q0=makeQuery(id+"F9.opExtrude","CAP_EDGE",EDGE,{"disambiguationData":[OSD([sQuery(id+"F8.wireOp",EDGE,"E33")])],"isStart":false});
            var Q1;
            Q1=makeQuery(id+"F9.opExtrude","CAP_EDGE",EDGE,{"disambiguationData":[OSD([sQuery(id+"F8.wireOp",EDGE,"E38")])],"isStart":false});
            chamfer(context, id + "F10", {"entities" : qUnion([Q0, Q1]), "chamferType" : ChamferType.TWO_OFFSETS, "width1" : 6 * mm, "oppositeDirection" : false, "width2" : 1.5 * mm, "tangentPropagation" : true});
        }
        {
            var Q0;
            Q0=makeQuery(id+"F9.opExtrude","CAP_EDGE",EDGE,{"disambiguationData":[OSD([sQuery(id+"F8.wireOp",EDGE,"E34")])],"isStart":false});
            var Q1;
            Q1=makeQuery(id+"F9.opExtrude","CAP_EDGE",EDGE,{"disambiguationData":[OSD([sQuery(id+"F8.wireOp",EDGE,"E39")])],"isStart":false});
            var Q2;
            Q2=makeQuery(id+"F9.opExtrude","CAP_EDGE",EDGE,{"disambiguationData":[OSD([sQuery(id+"F8.wireOp",EDGE,"E32")])],"isStart":false});
            var Q3;
            Q3=makeQuery(id+"F9.opExtrude","CAP_EDGE",EDGE,{"disambiguationData":[OSD([sQuery(id+"F8.wireOp",EDGE,"E28")])],"isStart":false});
            chamfer(context, id + "F11", {"entities" : qUnion([Q0, Q1, Q2, Q3]), "chamferType" : ChamferType.TWO_OFFSETS, "width1" : 6 * mm, "oppositeDirection" : false, "width2" : 2 * mm, "tangentPropagation" : true});
        }
        {
            var Q0;
            Q0=makeQuery(id+"F9.opExtrude","CAP_EDGE",EDGE,{"disambiguationData":[OSD([sQuery(id+"F8.wireOp",EDGE,"E35")])],"isStart":false});
            var Q1;
            Q1=makeQuery(id+"F9.opExtrude","CAP_EDGE",EDGE,{"disambiguationData":[OSD([sQuery(id+"F8.wireOp",EDGE,"E31")])],"isStart":false});
            chamfer(context, id + "F12", {"entities" : qUnion([Q0, Q1]), "chamferType" : ChamferType.TWO_OFFSETS, "width1" : 6 * mm, "oppositeDirection" : false, "width2" : 2.5 * mm, "tangentPropagation" : true});
        }
        {
            var Q0;
            Q0=makeQuery(id+"F9.opExtrude","CAP_EDGE",EDGE,{"disambiguationData":[OSD([sQuery(id+"F8.wireOp",EDGE,"E37")])],"isStart":false});
            var Q1;
            Q1=makeQuery(id+"F9.opExtrude","CAP_EDGE",EDGE,{"disambiguationData":[OSD([sQuery(id+"F8.wireOp",EDGE,"E36")])],"isStart":false});
            chamfer(context, id + "F13", {"entities" : qUnion([Q0, Q1]), "chamferType" : ChamferType.TWO_OFFSETS, "width1" : 6 * mm, "oppositeDirection" : false, "width2" : 3 * mm, "tangentPropagation" : true});
        }
        {
            var Q0;
            Q0=makeQuery(id+"F9.opExtrude","SWEPT_BODY",BODY,{"disambiguationData":[OSD([sQuery(id+"F8.wireOp",EDGE,"E28")])]});
            var Q1;
            Q1=makeQuery(id+"F9.opExtrude","SWEPT_BODY",BODY,{"disambiguationData":[OSD([sQuery(id+"F8.wireOp",EDGE,"E31")])]});
            var Q2;
            Q2=makeQuery(id+"F9.opExtrude","SWEPT_BODY",BODY,{"disambiguationData":[OSD([sQuery(id+"F8.wireOp",EDGE,"E33")])]});
            var Q3;
            Q3=makeQuery(id+"F9.opExtrude","SWEPT_BODY",BODY,{"disambiguationData":[OSD([sQuery(id+"F8.wireOp",EDGE,"E34")])]});
            var Q4;
            Q4=makeQuery(id+"F9.opExtrude","SWEPT_BODY",BODY,{"disambiguationData":[OSD([sQuery(id+"F8.wireOp",EDGE,"E35")])]});
            var Q5;
            Q5=makeQuery(id+"F9.opExtrude","SWEPT_BODY",BODY,{"disambiguationData":[OSD([sQuery(id+"F8.wireOp",EDGE,"E36")])]});
            var Q6;
            Q6=makeQuery(id+"F9.opExtrude","SWEPT_BODY",BODY,{"disambiguationData":[OSD([sQuery(id+"F8.wireOp",EDGE,"E37")])]});
            var Q7;
            Q7=makeQuery(id+"F9.opExtrude","SWEPT_BODY",BODY,{"disambiguationData":[OSD([sQuery(id+"F8.wireOp",EDGE,"E38")])]});
            var Q8;
            Q8=makeQuery(id+"F9.opExtrude","SWEPT_BODY",BODY,{"disambiguationData":[OSD([sQuery(id+"F8.wireOp",EDGE,"E39")])]});
            var Q9;
            Q9=makeQuery(id+"F9.opExtrude","SWEPT_BODY",BODY,{"disambiguationData":[OSD([sQuery(id+"F8.wireOp",EDGE,"E32")])]});
            var Q10;
            Q10=qCreatedBy(makeId("Front.planeOp"),FACE);
            mirror(context, id + "F14", {"entities" : qUnion([Q0, Q1, Q2, Q3, Q4, Q5, Q6, Q7, Q8, Q9]), "mirrorPlane" : qUnion([Q10])});
        }
        {
            var Q0;
            Q0=makeQuery(id+"F1.opExtrude","SWEPT_EDGE",EDGE,{"disambiguationData":[OSD([sQuery(id+"F0.wireOp",EDGE,"E1"),sQuery(id+"F0.wireOp",EDGE,"E2")])]});
            var Q1;
            Q1=makeQuery(id+"F1.opExtrude","SWEPT_EDGE",EDGE,{"disambiguationData":[OSD([sQuery(id+"F0.wireOp",EDGE,"E0"),sQuery(id+"F0.wireOp",EDGE,"E1")])]});
            chamfer(context, id + "F15", {"entities" : qUnion([Q0, Q1]), "width" : 0.7 * mm, "tangentPropagation" : true});
        }
        {
            var Q0;
            Q0=makeQuery(id+"F1.opExtrude","CAP_FACE",FACE,{"disambiguationData":[OSD([sQuery(id+"F0.wireOp",EDGE,"E0"),sQuery(id+"F0.wireOp",EDGE,"E1"),sQuery(id+"F0.wireOp",EDGE,"E2"),sQuery(id+"F0.wireOp",EDGE,"E3"),sQuery(id+"F0.wireOp",EDGE,"E4"),sQuery(id+"F0.wireOp",EDGE,"E5"),sQuery(id+"F0.wireOp",EDGE,"E6"),sQuery(id+"F0.wireOp",EDGE,"E7"),sQuery(id+"F0.wireOp",EDGE,"E8"),sQuery(id+"F0.wireOp",EDGE,"E9"),sQuery(id+"F0.wireOp",EDGE,"E10"),sQuery(id+"F0.wireOp",EDGE,"E14"),sQuery(id+"F0.wireOp",EDGE,"E15.filletArc"),sQuery(id+"F0.wireOp",EDGE,"E21"),sQuery(id+"F0.wireOp",EDGE,"E24")])],"isStart":true});
            var sketch = newSketch(context, id + "F16", { "sketchPlane" : qUnion([Q0])});
            skLineSegment(sketch, "E40.0", {"start": v(1, 0) * mm, "end": v(5, 6.67) * mm});
            skLineSegment(sketch, "E40.1", {"start": v(5, 6.67) * mm, "end": v(5, 32.34) * mm});
            skLineSegment(sketch, "E40.2", {"start": v(0, 0) * mm, "end": v(0, 39.3) * mm});
            skLineSegment(sketch, "E40.3", {"start": v(0, 0) * mm, "end": v(1, 0) * mm});
            skCircle(sketch, "E41", {"center": v(1, 0) * mm, "radius": 10 * mm});
            skArc(sketch, "E42", {"start": v(5, 11.67) * mm, "mid": v(5.48, 9.68) * mm, "end": v(6.82, 8.13) * mm});
            skArc(sketch, "E43", {"start": v(-1.8, 9.6) * mm, "mid": v(-0.5, 10.5) * mm, "end": v(0, 12) * mm});
            skSolve(sketch);
        }
        {
            var Q0;
            {var subQ0=sQuery(id+"F16.wireOp",EDGE,"E42");Q0=makeQuery(id+"F16.imprint","IMPRINT",FACE,{"disambiguationData":[TD([[makeQuery(id+"F16.imprint","IMPRINT",EDGE,{"derivedFrom":subQ0}),-1.0]])]});}
            var Q1;
            {var subQ5=sQuery(id+"F16.wireOp",EDGE,"E40.0");Q1=makeQuery(id+"F16.imprint","IMPRINT",FACE,{"disambiguationData":[TD([[makeQuery(id+"F16.imprint","IMPRINT",EDGE,{"derivedFrom":subQ5}),-1.0]])]});}
            var Q2;
            {var subQ0=sQuery(id+"F16.wireOp",EDGE,"E43");Q2=makeQuery(id+"F16.imprint","IMPRINT",FACE,{"disambiguationData":[TD([[makeQuery(id+"F16.imprint","IMPRINT",EDGE,{"derivedFrom":subQ0}),-1.0]])]});}
            extrude(context, id + "F17", {"entities" : qUnion([Q0, Q1, Q2]), "operationType" : NewBodyOperationType.ADD, "oppositeDirection" : true, "depth" : 0.5 * mm, "offsetDistance" : 25 * mm});
        }
    });
